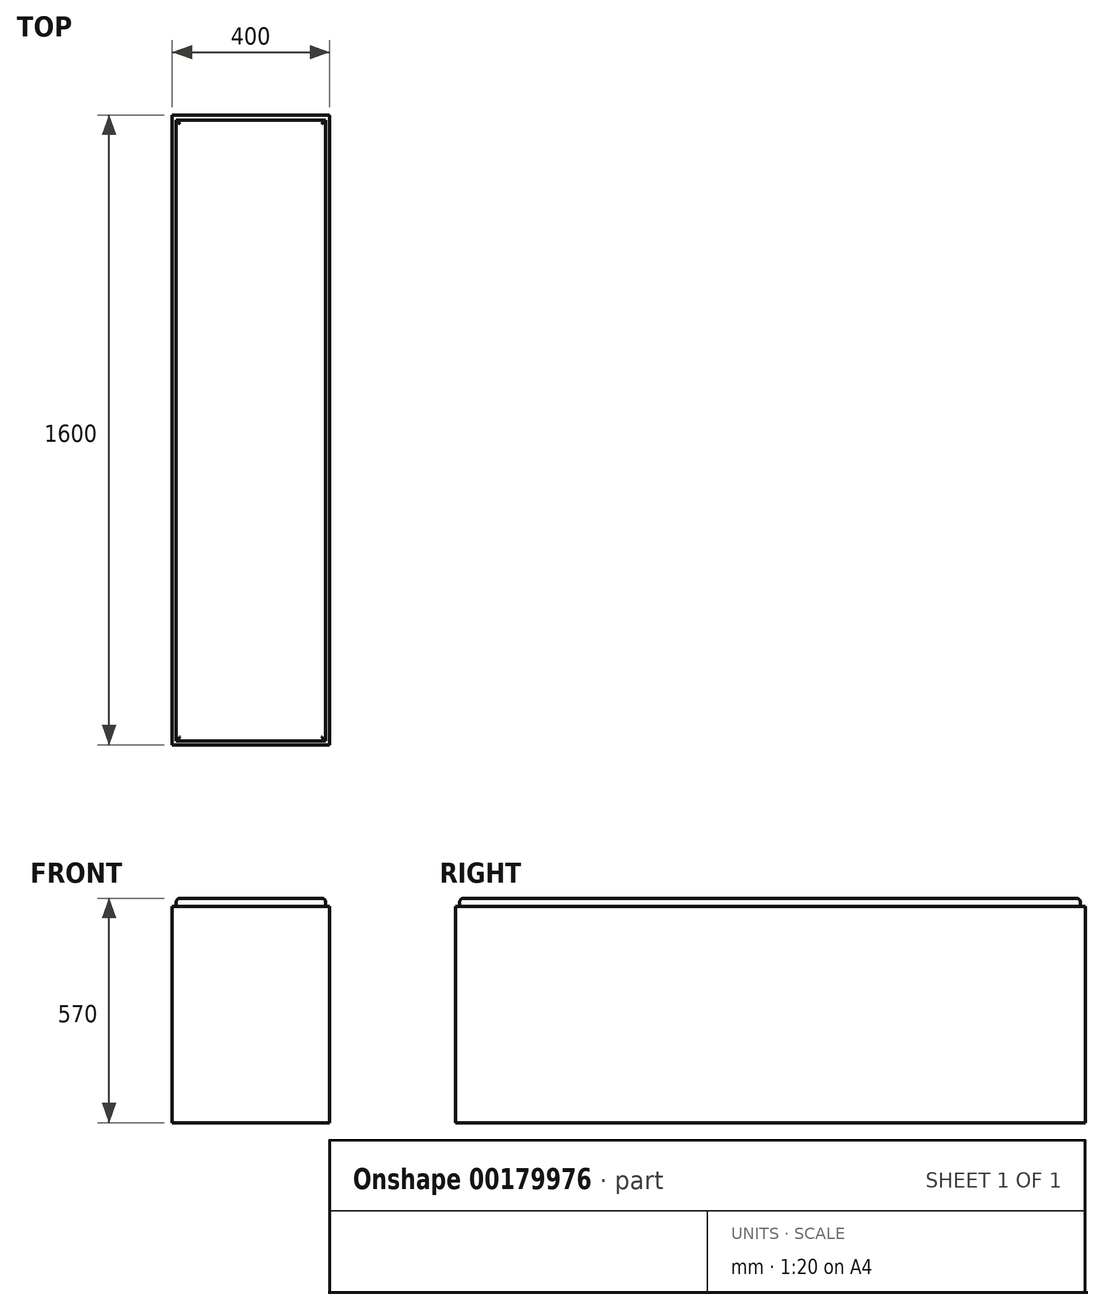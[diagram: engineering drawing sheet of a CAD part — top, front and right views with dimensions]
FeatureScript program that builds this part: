
annotation { "Feature Type Name" : "Feature", "Feature Type Description" : "" }
export const myFeature = defineFeature(function(context is Context, id is Id, definition is map)
    precondition{}
    {
        {
            var Q0;
            Q0=qCreatedBy(makeId("Front.planeOp"),FACE);
            var sketch = newSketch(context, id + "F0", { "sketchPlane" : qUnion([Q0])});
            skLineSegment(sketch, "E0.bottom", {"start": v(-205.17, 322.6) * mm, "end": v(194.83, 322.6) * mm});
            skLineSegment(sketch, "E0.top", {"start": v(-205.17, -227.4) * mm, "end": v(194.83, -227.4) * mm});
            skLineSegment(sketch, "E0.left", {"start": v(-205.17, 322.6) * mm, "end": v(-205.17, -227.4) * mm});
            skLineSegment(sketch, "E0.right", {"start": v(194.83, 322.6) * mm, "end": v(194.83, -227.4) * mm});
            skSolve(sketch);
        }
        {
            var Q0;
            Q0 = qSketchRegion(id + "F0", true);
            extrude(context, id + "F1", {"entities" : qUnion([Q0]), "depth" : 1600 * mm});
        }
        {
            var Q0;
            Q0=makeQuery(id+"F1.opExtrude","SWEPT_FACE",FACE,{"disambiguationData":[OSD([sQuery(id+"F0.wireOp",EDGE,"E0.bottom")])]});
            var sketch = newSketch(context, id + "F2", { "sketchPlane" : qUnion([Q0])});
            skLineSegment(sketch, "E1.bottom", {"start": v(-195.17, -12.7) * mm, "end": v(184.83, -12.7) * mm});
            skLineSegment(sketch, "E1.top", {"start": v(-195.17, -1590) * mm, "end": v(184.83, -1590) * mm});
            skLineSegment(sketch, "E1.left", {"start": v(-195.17, -12.7) * mm, "end": v(-195.17, -1590) * mm});
            skLineSegment(sketch, "E1.right", {"start": v(184.83, -12.7) * mm, "end": v(184.83, -1590) * mm});
            skSolve(sketch);
        }
        {
            var Q0;
            Q0 = qSketchRegion(id + "F2", true);
            extrude(context, id + "F3", {"entities" : qUnion([Q0]), "operationType" : NewBodyOperationType.ADD, "depth" : 20 * mm});
        }
        {
            var Q0;
            Q0=makeQuery(id+"F3.opExtrude","CAP_FACE",FACE,{"disambiguationData":[OSD([sQuery(id+"F2.wireOp",EDGE,"E1.bottom"),sQuery(id+"F2.wireOp",EDGE,"E1.top"),sQuery(id+"F2.wireOp",EDGE,"E1.left"),sQuery(id+"F2.wireOp",EDGE,"E1.right")])],"isStart":false});
            fillet(context, id + "F4", {"entities" : qUnion([Q0]), "radius" : 10 * mm, "tangentPropagation" : true, "allowEdgeOverflow" : false});
        }
    });
